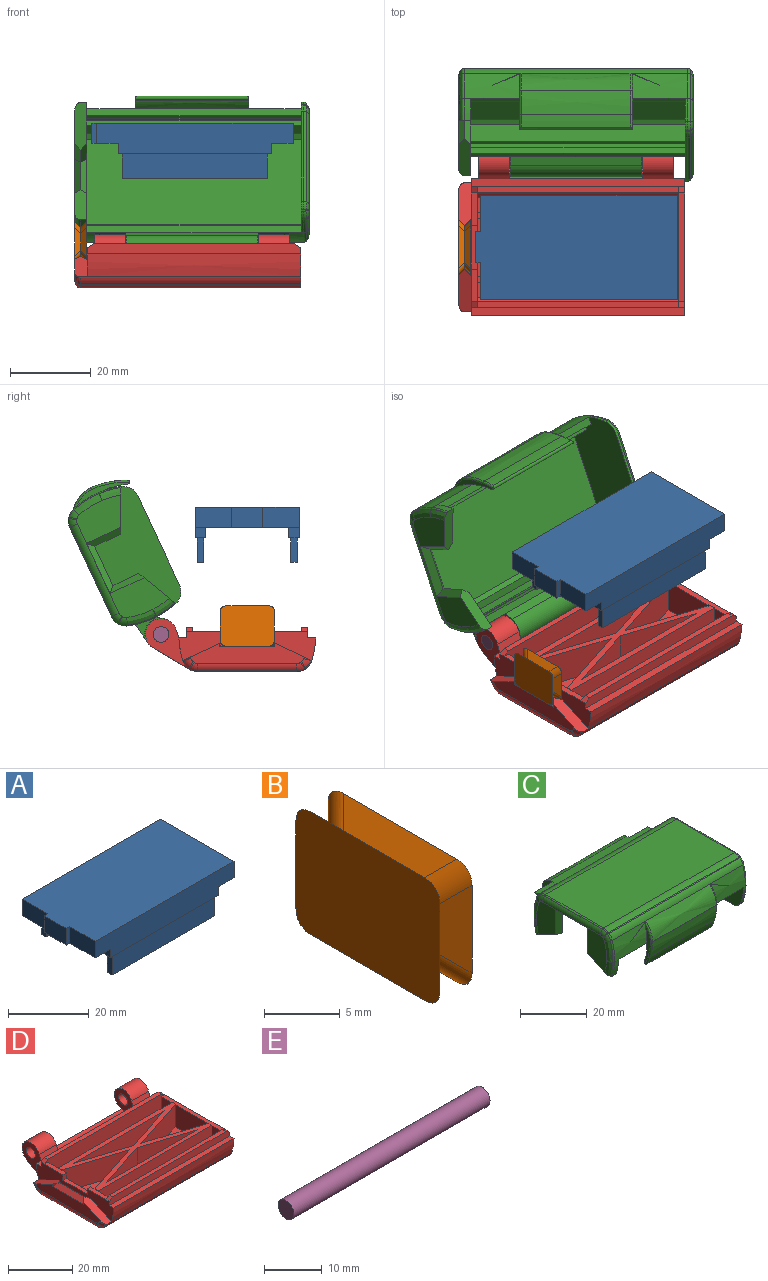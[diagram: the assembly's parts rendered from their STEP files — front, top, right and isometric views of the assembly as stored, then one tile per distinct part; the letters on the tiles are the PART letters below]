
ASSEMBLY  parts=5 mates=4
PART A: 28 faces, bbox 49.8x25.7x13.6 mm
  f0: plane 37.9x2.6mm, normal (0,0,-1), area 41.1mm2, adj f7,f12,f13,f14,f23,f24,f25,f26
  f1: plane 37.9x2.6mm, normal (0,0,-1), area 41.1mm2, adj f9,f15,f16,f17,f18,f19,f20,f21
  f2: plane 9x5mm, normal (-1,0,0), area 45mm2, adj f3,f9,f10,f11
  f3: plane 5x1.2mm, normal (0,1,0), area 6mm2, adj f2,f4,f10,f11
  f4: plane 7.7x5mm, normal (-1,0,0), area 38.5mm2, adj f3,f5,f10,f11
  f5: plane 5x1.2mm, normal (0,-1,0), area 6mm2, adj f4,f6,f10,f11
  f6: plane 9x5mm, normal (-1,0,0), area 45mm2, adj f5,f7,f10,f11
  f7: plane 48.6x7.6mm, normal (0,-1,0), area 341.5mm2, adj f0,f6,f8,f10,f11,f12,f14
  f8: plane 25.7x5mm, normal (1,0,0), area 128.5mm2, adj f7,f9,f10,f11
  f9: plane 48.6x7.6mm, normal (0,1,0), area 341.5mm2, adj f1,f2,f8,f10,f11,f15,f17
  f10: plane 49.8x25.7mm, normal (0,0,1), area 1258.3mm2, adj f2,f3,f4,f5,f6,f7,f8,f9
  f11: plane 49.8x25.7mm, normal (0,0,-1), area 1061.2mm2, adj f2,f3,f4,f5,f6,f7,f8,f9
  f12: plane 2.6x2.6mm, normal (-1,0,0), area 6.8mm2, adj f0,f7,f11,f13
  f13: plane 37.9x2.6mm, normal (0,1,0), area 98.5mm2, adj f0,f11,f12,f14
  f14: plane 2.6x2.6mm, normal (1,0,0), area 6.8mm2, adj f0,f7,f11,f13
  f15: plane 2.6x2.6mm, normal (1,0,0), area 6.8mm2, adj f1,f9,f11,f16
  f16: plane 37.9x2.6mm, normal (0,-1,0), area 98.5mm2, adj f1,f11,f15,f17
  f17: plane 2.6x2.6mm, normal (-1,0,0), area 6.8mm2, adj f1,f9,f11,f16
  f18: plane 6x1.6mm, normal (1,0,0), area 9.6mm2, adj f1,f19,f21,f22
  f19: plane 35.9x6mm, normal (0,-1,0), area 215.4mm2, adj f1,f18,f20,f22
  f20: plane 6x1.6mm, normal (-1,0,0), area 9.6mm2, adj f1,f19,f21,f22
  f21: plane 35.9x6mm, normal (0,1,0), area 215.4mm2, adj f1,f18,f20,f22
  f22: plane 35.9x1.6mm, normal (0,0,-1), area 57.4mm2, adj f18,f19,f20,f21
  f23: plane 6x1.6mm, normal (1,0,0), area 9.6mm2, adj f0,f24,f26,f27
  f24: plane 35.9x6mm, normal (0,-1,0), area 215.4mm2, adj f0,f23,f25,f27
  f25: plane 6x1.6mm, normal (-1,0,0), area 9.6mm2, adj f0,f24,f26,f27
  f26: plane 35.9x6mm, normal (0,1,0), area 215.4mm2, adj f0,f23,f25,f27
  f27: plane 35.9x1.6mm, normal (0,0,-1), area 57.4mm2, adj f23,f24,f25,f26
PART B: 23 faces, bbox 3.4x13.9x10.4 mm
  f0: plane 13.42x9.92mm, normal (-1,0,0), area 131.6mm2, adj f5,f6,f7,f8,f11,f13,f14,f16
  f1: plane 10.59x1.5mm, normal (-0.71,0,0.71), area 19.3mm2, adj f5,f9,f10,f12
  f2: plane 7.09x1.5mm, normal (-0.71,-0.71,0), area 11.9mm2, adj f6,f9,f12,f17
  f3: plane 7.09x1.5mm, normal (-0.71,0.71,0), area 11.9mm2, adj f7,f9,f10,f15
  f4: plane 10.59x1.5mm, normal (-0.71,0,-0.71), area 19.3mm2, adj f8,f9,f15,f17
  f5: plane 10.59x1.5mm, normal (0.71,0,0.71), area 19.3mm2, adj f0,f1,f11,f13
  f6: plane 7.09x1.5mm, normal (0.71,-0.71,0), area 11.9mm2, adj f0,f2,f13,f16
  f7: plane 7.09x1.5mm, normal (0.71,0.71,0), area 11.9mm2, adj f0,f3,f11,f14
  f8: plane 10.59x1.5mm, normal (0.71,0,-0.71), area 19.3mm2, adj f0,f4,f14,f16
  f9: plane 13.42x9.92mm, normal (1,0,0), area 51.1mm2, adj f1,f2,f3,f4,f10,f12,f15,f17
  f10: cylinder r=2mm len=3.13mm, axis (-0.58,-0.58,-0.58), area 5.4mm2, adj f1,f3,f9,f11
  f11: cylinder r=2mm len=3.13mm, axis (-0.58,0.58,0.58), area 5.4mm2, adj f0,f5,f7,f10
  f12: cylinder r=2mm len=3.13mm, axis (-0.58,0.58,-0.58), area 5.4mm2, adj f1,f2,f9,f13
  f13: cylinder r=2mm len=3.13mm, axis (-0.58,-0.58,0.58), area 5.4mm2, adj f0,f5,f6,f12
  f14: cylinder r=2mm len=3.13mm, axis (0.58,-0.58,0.58), area 5.4mm2, adj f0,f7,f8,f15
  f15: cylinder r=2mm len=3.13mm, axis (0.58,0.58,-0.58), area 5.4mm2, adj f3,f4,f9,f14
  f16: cylinder r=2mm len=3.13mm, axis (0.58,0.58,0.58), area 5.4mm2, adj f0,f6,f8,f17
  f17: cylinder r=2mm len=3.13mm, axis (0.58,-0.58,-0.58), area 5.4mm2, adj f2,f4,f9,f16
  f18: plane 7.4x0.75mm, normal (0.71,-0.71,0), area 7.1mm2, adj f9,f19,f21,f22
  f19: plane 9.37x5.9mm, normal (1,0,0), area 55.3mm2, adj f18,f20,f21,f22
  f20: plane 7.4x0.75mm, normal (0.71,0.71,0), area 7.1mm2, adj f9,f19,f21,f22
  f21: plane 10.87x0.75mm, normal (0.71,0,0.71), area 10.7mm2, adj f9,f18,f19,f20
  f22: plane 10.87x0.75mm, normal (0.71,0,-0.71), area 10.7mm2, adj f9,f18,f19,f20
PART C: 183 faces, bbox 58x44.2x23.5 mm
  f0: extruded ~55.38x7.38mm, area 142.9mm2, adj f15,f20,f36,f40,f92,f105,f172,f178
  f1: extruded ~14.19x7.37mm, area 102.5mm2, adj f13,f23,f26,f77,f147,f159
  f2: extruded ~14.19x7.37mm, area 102.5mm2, adj f13,f23,f43,f96,f155,f165
  f3: plane 29.75x12.79mm, normal (-1,0,0), area 170.4mm2, adj f126,f127,f128,f129,f130,f131,f132,f133
  f4: plane 53x1mm, normal (0,-1,0), area 53mm2, adj f5,f17,f38,f39
  f5: plane 53x1.5mm, normal (0,0,-1), area 79.5mm2, adj f4,f6,f38,f39
  f6: plane 53x4.6mm, normal (0,-1,0), area 243.8mm2, adj f5,f25,f38,f39
  f7: plane 53x24.9mm, normal (0,0,-1), area 1319.7mm2, adj f24,f25,f38,f39
  f8: plane 53x4.6mm, normal (0,1,0), area 243.8mm2, adj f9,f24,f38,f39
  f9: plane 53x1.5mm, normal (0,0,-1), area 79.5mm2, adj f8,f10,f38,f39
  f10: plane 53x1mm, normal (0,1,0), area 53mm2, adj f9,f11,f38,f39
  f11: plane 53x0.1mm, normal (0,0,-1), area 5.3mm2, adj f10,f12,f38,f39
  f12: plane 53x1.5mm, normal (0,1,0), area 79.5mm2, adj f11,f13,f38,f39
  f13: plane 53x1.89mm, normal (0,0,-1), area 99.9mm2, adj f1,f2,f12,f38,f39,f149
  f14: plane 55.38x24.51mm, normal (0,0,1), area 1357.2mm2, adj f21,f22,f84,f100
  f15: plane 53x1.88mm, normal (0,0,-1), area 99.9mm2, adj f0,f16,f38,f39,f174
  f16: plane 53x1.52mm, normal (0,-1,0), area 80.5mm2, adj f15,f17,f38,f39
  f17: plane 53x0.1mm, normal (0,0,-1), area 5.3mm2, adj f4,f16,f38,f39
  f18: plane 55.38x0.22mm, normal (0,-0.57,0.82), area 15.1mm2, adj f21,f23,f80,f98
  f19: plane 55.38x0.22mm, normal (0,0.57,0.82), area 15.1mm2, adj f20,f22,f88,f102
  f20: cylinder r=3.63mm len=55.38mm, axis (-1,0,0), area 133.5mm2, adj f0,f19,f90,f104
  f21: cylinder r=3.63mm len=55.38mm, axis (1,0,0), area 123.2mm2, adj f14,f18,f82,f99
  f22: cylinder r=3.63mm len=55.38mm, axis (-1,0,0), area 123.2mm2, adj f14,f19,f86,f101
  f23: cylinder r=3.63mm len=55.38mm, axis (-1,0,0), area 133.5mm2, adj f1,f2,f18,f78,f97,f150
  f24: plane 53x1mm, normal (0,0.71,-0.71), area 75mm2, adj f7,f8,f38,f39
  f25: plane 53x1mm, normal (0,-0.71,-0.71), area 75mm2, adj f6,f7,f38,f39
  f26: plane 0.71x0.11mm, normal (0,-1,-0.04), area 0.1mm2, adj f1,f27,f38,f77,f79
  f27: extruded ~5.67x0.98mm, area 4mm2, adj f26,f28,f38,f79
  f28: cylinder r=3.63mm len=1.92mm, axis (-1,0,0), area 1.7mm2, adj f27,f29,f38,f81
  f29: plane 0.69x0.22mm, normal (0,-0.57,-0.82), area 0.2mm2, adj f28,f30,f38,f83
  f30: cylinder r=3.63mm len=2.09mm, axis (-1,0,0), area 1.5mm2, adj f29,f31,f38,f85
  f31: plane 24.51x0.69mm, normal (0,0,-1), area 16.9mm2, adj f30,f32,f38,f87
  f32: cylinder r=3.63mm len=2.09mm, axis (-1,0,0), area 1.5mm2, adj f31,f33,f38,f89
  f33: plane 0.69x0.22mm, normal (0,0.57,-0.82), area 0.2mm2, adj f32,f34,f38,f91
  f34: cylinder r=3.63mm len=1.92mm, axis (-1,0,0), area 1.7mm2, adj f33,f35,f38,f93
  f35: extruded ~5.67x0.98mm, area 4mm2, adj f34,f36,f38,f94
  f36: plane 0.71x0.09mm, normal (0,1,-0.04), area 0.1mm2, adj f0,f35,f38,f92,f94
  f37: plane 29.75x14.45mm, normal (1,0,0), area 415.5mm2, adj f106,f107,f108,f109,f110,f111,f112,f113
  f38: plane 33.87x16.6mm, normal (-1,0,0), area 497.5mm2, adj f4,f5,f6,f7,f8,f9,f10,f11
  f39: plane 33.87x13.84mm, normal (1,0,0), area 185.6mm2, adj f4,f5,f6,f7,f8,f9,f10,f11
  f40: plane 1.71x0.09mm, normal (0,1,-0.04), area 0.1mm2, adj f0,f39,f41,f103,f105
  f41: extruded ~5.57x1.69mm, area 9.6mm2, adj f39,f40,f103,f146
  f42: extruded ~5.57x1.69mm, area 9.6mm2, adj f39,f43,f95,f145
  f43: plane 1.71x0.11mm, normal (0,-1,-0.04), area 0.2mm2, adj f2,f39,f42,f95,f96
  f44: plane 0.08x0.03mm, normal (-0.71,0.71,-0.03), area 0mm2, adj f45,f46,f103,f105,f131
  f45: bspline ~5.71x1.94mm, area 0.1mm2, adj f44,f103,f133,f146
  f46: bspline ~7.38x2.04mm, area 0.1mm2, adj f44,f105,f129
  f47: cone r=2.63mm half-angle=45deg, axis (1,0,0), area 0.1mm2, adj f48,f104,f127
  f48: plane 0.23x0.17mm, normal (-0.71,0.41,0.58), area 0mm2, adj f47,f49,f102,f126
  f49: cone r=2.63mm half-angle=45deg, axis (1,0,0), area 0.1mm2, adj f48,f50,f101,f128
  f50: plane 24.51x0.02mm, normal (-0.71,0,0.71), area 0.7mm2, adj f49,f51,f100,f130
  f51: cone r=2.63mm half-angle=45deg, axis (1,0,0), area 0.1mm2, adj f50,f52,f99,f132
  f52: plane 0.23x0.17mm, normal (-0.71,-0.41,0.58), area 0mm2, adj f51,f53,f98,f134
  f53: cone r=2.63mm half-angle=45deg, axis (1,0,0), area 0mm2, adj f52,f97,f135
  f54: bspline ~5.71x1.94mm, area 0.1mm2, adj f95,f138,f145
  f55: bspline ~7.37x2.03mm, area 0mm2, adj f96,f136
  f56: plane 0.11x0.03mm, normal (-0.71,-0.71,-0.03), area 0mm2, adj f95,f96,f137
  f57: plane 0.11x0.03mm, normal (0.71,-0.71,-0.03), area 0mm2, adj f77,f79,f123
  f58: bspline ~5.71x1.94mm, area 0mm2, adj f79,f125
  f59: bspline ~7.37x2.03mm, area 0mm2, adj f77,f121
  f60: cone r=2.63mm half-angle=45deg, axis (-1,0,0), area 0mm2, adj f62,f81,f124
  f61: cone r=2.63mm half-angle=45deg, axis (-1,0,0), area 0.1mm2, adj f63,f78,f119
  f62: plane 0.23x0.17mm, normal (0.71,-0.41,-0.58), area 0mm2, adj f60,f64,f83,f122
  f63: plane 0.23x0.17mm, normal (0.71,-0.41,0.58), area 0mm2, adj f61,f65,f80,f117
  f64: cone r=2.63mm half-angle=45deg, axis (-1,0,0), area 0.1mm2, adj f62,f66,f85,f120
  f65: cone r=2.63mm half-angle=45deg, axis (-1,0,0), area 0.1mm2, adj f63,f67,f82,f115
  f66: plane 24.51x0.02mm, normal (0.71,0,-0.71), area 0.7mm2, adj f64,f68,f87,f118
  f67: plane 24.51x0.02mm, normal (0.71,0,0.71), area 0.7mm2, adj f65,f69,f84,f113
  f68: cone r=2.63mm half-angle=45deg, axis (-1,0,0), area 0.1mm2, adj f66,f70,f89,f116
  f69: cone r=2.63mm half-angle=45deg, axis (-1,0,0), area 0.1mm2, adj f67,f71,f86,f111
  f70: plane 0.23x0.17mm, normal (0.71,0.41,-0.58), area 0mm2, adj f68,f72,f91,f114
  f71: plane 0.23x0.17mm, normal (0.71,0.41,0.58), area 0mm2, adj f69,f73,f88,f109
  f72: cone r=2.63mm half-angle=45deg, axis (-1,0,0), area 0.1mm2, adj f70,f93,f112
  f73: cone r=2.63mm half-angle=45deg, axis (-1,0,0), area 0mm2, adj f71,f90,f107
  f74: bspline ~5.71x1.94mm, area 0.1mm2, adj f76,f94,f110
  f75: bspline ~7.38x2.04mm, area 0.1mm2, adj f76,f92,f106
  f76: plane 0.09x0.03mm, normal (0.71,0.71,-0.03), area 0mm2, adj f74,f75,f92,f94,f108
  f77: bspline ~7.94x1.28mm, area 4.4mm2, adj f1,f26,f57,f59,f78,f79
  f78: torus R=2.88mm, axis (1,0,0), area 1.4mm2, adj f23,f61,f77,f80
  f79: bspline ~7.33x1.52mm, area 3.4mm2, adj f26,f27,f57,f58,f77,f81
  f80: cylinder r=0.75mm len=0.53mm, axis (0,-0.82,-0.57), area 0.2mm2, adj f18,f63,f78,f82
  f81: torus R=2.88mm, axis (1,0,0), area 1.4mm2, adj f28,f60,f79,f83
  f82: torus R=2.88mm, axis (1,0,0), area 1.3mm2, adj f21,f65,f80,f84
  f83: cylinder r=0.75mm len=0.53mm, axis (0,0.82,-0.57), area 0.2mm2, adj f29,f62,f81,f85
  f84: cylinder r=0.75mm len=24.51mm, axis (0,-1,0), area 14.4mm2, adj f14,f67,f82,f86
  f85: torus R=2.88mm, axis (1,0,0), area 1.3mm2, adj f30,f64,f83,f87
  f86: torus R=2.88mm, axis (1,0,0), area 1.3mm2, adj f22,f69,f84,f88
  f87: cylinder r=0.75mm len=24.51mm, axis (0,1,0), area 14.4mm2, adj f31,f66,f85,f89
  f88: cylinder r=0.75mm len=0.53mm, axis (0,-0.82,0.57), area 0.2mm2, adj f19,f71,f86,f90
  f89: torus R=2.88mm, axis (1,0,0), area 1.3mm2, adj f32,f68,f87,f91
  f90: torus R=2.88mm, axis (1,0,0), area 1.4mm2, adj f20,f73,f88,f92
  f91: cylinder r=0.75mm len=0.53mm, axis (0,0.82,0.57), area 0.2mm2, adj f33,f70,f89,f93
  f92: bspline ~8.64x1.51mm, area 4.4mm2, adj f0,f36,f75,f76,f90,f94
  f93: torus R=2.88mm, axis (1,0,0), area 1.4mm2, adj f34,f72,f91,f94
  f94: bspline ~7.35x1.4mm, area 3.4mm2, adj f35,f36,f74,f76,f92,f93
  f95: bspline ~7.35x1.4mm, area 3.3mm2, adj f42,f43,f54,f56,f96,f145
  f96: bspline ~7.94x1.28mm, area 4.4mm2, adj f2,f43,f55,f56,f95,f97
  f97: torus R=2.88mm, axis (-1,0,0), area 1.4mm2, adj f23,f53,f96,f98
  f98: cylinder r=0.75mm len=0.53mm, axis (0,0.82,0.57), area 0.2mm2, adj f18,f52,f97,f99
  f99: torus R=2.88mm, axis (-1,0,0), area 1.3mm2, adj f21,f51,f98,f100
  f100: cylinder r=0.75mm len=24.51mm, axis (0,1,0), area 14.4mm2, adj f14,f50,f99,f101
  f101: torus R=2.88mm, axis (-1,0,0), area 1.3mm2, adj f22,f49,f100,f102
  f102: cylinder r=0.75mm len=0.53mm, axis (0,0.82,-0.57), area 0.2mm2, adj f19,f48,f101,f104
  f103: bspline ~7.33x1.52mm, area 3.3mm2, adj f40,f41,f44,f45,f105,f146
  f104: torus R=2.88mm, axis (-1,0,0), area 1.4mm2, adj f20,f47,f102,f105
  f105: bspline ~8.65x1.51mm, area 4.4mm2, adj f0,f40,f44,f46,f103,f104
  f106: bspline ~9.59x3.35mm, area 14.5mm2, adj f37,f75,f107,f108
  f107: torus R=1.56mm, axis (1,0,0), area 3.4mm2, adj f37,f73,f106,f109
  f108: cylinder r=2.6mm len=1.84mm, axis (0,0.04,1), area 0.2mm2, adj f37,f76,f106,f110
  f109: cylinder r=2.6mm len=1.66mm, axis (0,-0.82,0.57), area 0.6mm2, adj f37,f71,f107,f111
  f110: bspline ~7.45x3.19mm, area 11.2mm2, adj f37,f74,f108,f112
  f111: torus R=1.56mm, axis (1,0,0), area 3.2mm2, adj f37,f69,f109,f113
  f112: torus R=1.56mm, axis (1,0,0), area 3.4mm2, adj f37,f72,f110,f114
  f113: cylinder r=2.6mm len=24.51mm, axis (0,-1,0), area 50mm2, adj f37,f67,f111,f115
  f114: cylinder r=2.6mm len=1.66mm, axis (0,0.82,0.57), area 0.6mm2, adj f37,f70,f112,f116
  f115: torus R=1.56mm, axis (1,0,0), area 3.2mm2, adj f37,f65,f113,f117
  f116: torus R=1.56mm, axis (1,0,0), area 3.2mm2, adj f37,f68,f114,f118
  f117: cylinder r=2.6mm len=1.66mm, axis (0,-0.82,-0.57), area 0.6mm2, adj f37,f63,f115,f119
  f118: cylinder r=2.6mm len=24.51mm, axis (0,1,0), area 50mm2, adj f37,f66,f116,f120
  f119: torus R=1.56mm, axis (1,0,0), area 3.4mm2, adj f37,f61,f117,f121
  f120: torus R=1.56mm, axis (1,0,0), area 3.2mm2, adj f37,f64,f118,f122
  f121: bspline ~9.61x3.35mm, area 14.5mm2, adj f37,f59,f119,f123
  f122: cylinder r=2.6mm len=1.66mm, axis (0,0.82,-0.57), area 0.6mm2, adj f37,f62,f120,f124
  f123: cylinder r=2.6mm len=1.84mm, axis (0,-0.04,1), area 0.2mm2, adj f37,f57,f121,f125
  f124: torus R=1.56mm, axis (1,0,0), area 3.4mm2, adj f37,f60,f122,f125
  f125: bspline ~7.47x3.19mm, area 11.2mm2, adj f37,f58,f123,f124
  f126: cylinder r=2.6mm len=1.66mm, axis (0,0.82,-0.57), area 0.6mm2, adj f3,f48,f127,f128
  f127: torus R=1.56mm, axis (-1,0,0), area 3.4mm2, adj f3,f47,f126,f129
  f128: torus R=1.56mm, axis (-1,0,0), area 3.2mm2, adj f3,f49,f126,f130
  f129: bspline ~11.34x3.35mm, area 14.5mm2, adj f3,f46,f127,f131
  f130: cylinder r=2.6mm len=24.51mm, axis (0,1,0), area 50mm2, adj f3,f50,f128,f132
  f131: cylinder r=2.6mm len=1.84mm, axis (0,0.04,1), area 0.2mm2, adj f3,f44,f129,f133
  f132: torus R=1.56mm, axis (-1,0,0), area 3.2mm2, adj f3,f51,f130,f134
  f133: bspline ~6.97x2.84mm, area 10.6mm2, adj f3,f45,f131,f146
  f134: cylinder r=2.6mm len=1.66mm, axis (0,0.82,0.57), area 0.6mm2, adj f3,f52,f132,f135
  f135: torus R=1.56mm, axis (-1,0,0), area 3.4mm2, adj f3,f53,f134,f136
  f136: bspline ~11.33x3.36mm, area 14.5mm2, adj f3,f55,f135,f137
  f137: cylinder r=2.6mm len=1.84mm, axis (0,-0.04,1), area 0.2mm2, adj f3,f56,f136,f138
  f138: bspline ~6.96x2.84mm, area 10.6mm2, adj f3,f54,f137,f145
  f139: plane 13.7x1.5mm, normal (-0.71,0,-0.71), area 25.9mm2, adj f3,f140,f141,f142
  f140: plane 9.31x1.5mm, normal (-0.71,0.71,0), area 17.4mm2, adj f3,f139,f143,f145
  f141: plane 9.31x1.5mm, normal (-0.71,-0.71,0), area 17.4mm2, adj f3,f139,f144,f146
  f142: plane 13.7x1.5mm, normal (0.71,0,-0.71), area 25.9mm2, adj f39,f139,f143,f144
  f143: plane 9.31x1.5mm, normal (0.71,0.71,0), area 17.4mm2, adj f39,f140,f142,f145
  f144: plane 9.31x1.5mm, normal (0.71,-0.71,0), area 17.4mm2, adj f39,f141,f142,f146
  f145: plane 10.67x5.12mm, normal (0,0.43,-0.9), area 32.2mm2, adj f3,f39,f42,f54,f95,f138,f140,f143
  f146: plane 10.67x5.11mm, normal (0,-0.43,-0.9), area 32.2mm2, adj f3,f39,f41,f45,f103,f133,f141,f144
  f147: plane 14.5x2.63mm, normal (1,0,0), area 14.2mm2, adj f1,f148,f149,f157,f159,f160,f161,f162
  f148: plane 28x0.01mm, normal (0,0.94,0.33), area 0.4mm2, adj f147,f149,f155,f157
  f149: extruded ~28x7.38mm, area 210.2mm2, adj f13,f147,f148,f155
  f150: extruded ~27x6.04mm, area 186.2mm2, adj f23,f151,f159,f165
  f151: plane 27x0.04mm, normal (0,-1,-0.04), area 0.9mm2, adj f150,f152,f160,f166
  f152: plane 27x0.04mm, normal (0,-1,-0.04), area 1.2mm2, adj f151,f153,f161,f167
  f153: plane 27x0mm, normal (0,-1,-0.04), area 0mm2, adj f152,f154,f162,f168
  f154: extruded ~27x6.09mm, area 167.1mm2, adj f153,f156,f163,f169
  f155: plane 14.5x2.63mm, normal (-1,0,0), area 14.2mm2, adj f2,f148,f149,f157,f165,f166,f167,f168
  f156: extruded ~27x2.93mm, area 84.9mm2, adj f154,f158,f164,f170
  f157: cylinder r=0.5mm len=28mm, axis (-1,0,0), area 43.5mm2, adj f147,f148,f155,f158,f164,f170
  f158: plane 27.08x0mm, normal (0,0.38,-0.92), area 0mm2, adj f156,f157,f164,f170
  f159: bspline ~6.65x3.7mm, area 4.9mm2, adj f1,f147,f150,f160
  f160: cylinder r=0.5mm len=0.5mm, axis (0,-0.04,1), area 0mm2, adj f147,f151,f159,f161
  f161: cylinder r=0.5mm len=0.5mm, axis (0,-0.04,1), area 0mm2, adj f147,f152,f160,f162
  f162: cylinder r=0.5mm len=0.5mm, axis (0,-0.04,1), area 0mm2, adj f147,f153,f161,f163
  f163: bspline ~15.73x4.09mm, area 4.8mm2, adj f147,f154,f162,f164
  f164: bspline ~5.71x2.71mm, area 2.7mm2, adj f147,f156,f157,f158,f163
  f165: bspline ~6.65x3.7mm, area 4.9mm2, adj f2,f150,f155,f166
  f166: cylinder r=0.5mm len=0.5mm, axis (0,0.04,-1), area 0mm2, adj f151,f155,f165,f167
  f167: cylinder r=0.5mm len=0.5mm, axis (0,0.04,-1), area 0mm2, adj f152,f155,f166,f168
  f168: cylinder r=0.5mm len=0.5mm, axis (0,0.04,-1), area 0mm2, adj f153,f155,f167,f169
  f169: bspline ~15.73x4.09mm, area 4.8mm2, adj f154,f155,f168,f170
  f170: bspline ~5.71x2.71mm, area 2.7mm2, adj f155,f156,f157,f158,f169
  f171: plane 8.25x7.91mm, normal (1,0,0), area 37.3mm2, adj f172,f173,f174,f179,f180,f182
  f172: plane 48x5.58mm, normal (0,0.17,0.98), area 252.6mm2, adj f0,f171,f173,f175,f177,f178,f179,f181
  f173: cylinder r=3.88mm len=32.6mm, axis (-1,0,0), area 484.2mm2, adj f171,f172,f174,f175
  f174: plane 48x1.69mm, normal (0,-0.76,-0.65), area 72.7mm2, adj f15,f171,f173,f175,f176,f178,f180,f181
  f175: plane 8.25x7.91mm, normal (-1,0,0), area 37.3mm2, adj f172,f173,f174,f176,f177,f182
  f176: plane 7.7x1.76mm, normal (0,0.97,-0.23), area 13.9mm2, adj f174,f175,f177,f178
  f177: cylinder r=4.07mm len=7.7mm, axis (-1,0,0), area 37.7mm2, adj f172,f175,f176,f178
  f178: plane 5.63x4.34mm, normal (-1,0,0), area 6.8mm2, adj f0,f172,f174,f176,f177
  f179: cylinder r=4.07mm len=7.7mm, axis (-1,0,0), area 37.7mm2, adj f171,f172,f180,f181
  f180: plane 7.7x1.76mm, normal (0,0.97,-0.23), area 13.9mm2, adj f171,f174,f179,f181
  f181: plane 5.63x4.34mm, normal (1,0,0), area 6.8mm2, adj f0,f172,f174,f179,f180
  f182: cylinder r=1.94mm len=32.6mm, axis (-1,0,0), area 396.9mm2, adj f171,f175
PART D: 113 faces, bbox 55.9x42.2x13.5 mm
  f0: plane 48x2.14mm, normal (0,-0.95,0.32), area 36mm2, adj f1,f2,f27,f105,f106,f107,f109,f110
  f1: cylinder r=3.88mm len=7.55mm, axis (-1,0,0), area 112mm2, adj f0,f3,f106,f107
  f2: cylinder r=3.88mm len=7.55mm, axis (-1,0,0), area 112mm2, adj f0,f3,f105,f109
  f3: plane 48x8.85mm, normal (0,0.51,-0.86), area 451.7mm2, adj f1,f2,f36,f105,f106,f107,f108,f109
  f4: extruded ~5.67x2.9mm, area 16.7mm2, adj f5,f20,f27,f105
  f5: cylinder r=3.63mm len=2.9mm, axis (-1,0,0), area 7mm2, adj f4,f20,f36,f105
  f6: plane 14.5x8.4mm, normal (1,0,0), area 99.3mm2, adj f13,f14,f16,f44,f45,f46,f94,f95
  f7: plane 8.4x4.7mm, normal (1,0,0), area 39mm2, adj f11,f14,f23,f43,f96
  f8: plane 8.4x4.7mm, normal (-1,0,0), area 39mm2, adj f11,f15,f23,f43,f96
  f9: plane 14.5x8.4mm, normal (-1,0,0), area 121.8mm2, adj f10,f15,f97,f98
  f10: plane 22.46x14.5mm, normal (0,0,1), area 162.8mm2, adj f9,f97,f98
  f11: plane 49.8x3.7mm, normal (0,0,1), area 184.3mm2, adj f7,f8,f43,f96
  f12: plane 49.8x3.7mm, normal (0,0,1), area 184.3mm2, adj f22,f24,f42,f93
  f13: plane 22.46x14.5mm, normal (0,0,1), area 162.8mm2, adj f6,f94,f95
  f14: plane 8.1x1.5mm, normal (0,0,1), area 12.2mm2, adj f6,f7,f18,f23,f46,f87
  f15: plane 26.9x1.5mm, normal (0,0,1), area 40.4mm2, adj f8,f9,f20,f23,f24,f25,f88,f89
  f16: plane 8.1x1.5mm, normal (0,0,1), area 12.2mm2, adj f6,f18,f22,f25,f44,f86
  f17: plane 52.8x2.5mm, normal (0,-1,0), area 130.5mm2, adj f18,f20,f29,f31,f34,f35
  f18: plane 33.86x7.24mm, normal (-1,0,0), area 121.7mm2, adj f14,f16,f17,f19,f26,f27,f28,f29
  f19: plane 52.8x2.5mm, normal (0,1,0), area 130.5mm2, adj f18,f20,f27,f30,f32,f33
  f20: plane 33.86x9.9mm, normal (1,0,0), area 314.3mm2, adj f4,f5,f15,f17,f19,f21,f27,f28
  f21: plane 54.59x24.51mm, normal (0,0,-1), area 1337.8mm2, adj f20,f40,f41,f63
  f22: plane 8.4x4.7mm, normal (1,0,0), area 39mm2, adj f12,f16,f25,f42,f93
  f23: plane 52.8x8.4mm, normal (0,1,0), area 419.8mm2, adj f7,f8,f14,f15,f31,f34,f35,f43
  f24: plane 8.4x4.7mm, normal (-1,0,0), area 39mm2, adj f12,f15,f25,f42,f93
  f25: plane 52.8x8.4mm, normal (0,-1,0), area 419.8mm2, adj f15,f16,f22,f24,f30,f32,f33,f42
  f26: extruded ~5.67x1.9mm, area 11mm2, adj f18,f27,f39,f106
  f27: plane 52.8x1.98mm, normal (0,0,1), area 104.6mm2, adj f0,f4,f18,f19,f20,f26
  f28: extruded ~52.8x5.67mm, area 304.4mm2, adj f18,f20,f29,f38
  f29: plane 52.8x1.98mm, normal (0,0,1), area 104.6mm2, adj f17,f18,f20,f28
  f30: plane 49.8x1.5mm, normal (0,0,1), area 74.7mm2, adj f19,f25,f32,f33
  f31: plane 49.8x1.5mm, normal (0,0,1), area 74.7mm2, adj f17,f23,f34,f35
  f32: plane 1.5x1.5mm, normal (0.55,0,0.83), area 2.7mm2, adj f19,f20,f25,f30
  f33: plane 1.5x1.5mm, normal (-0.55,0,0.83), area 2.7mm2, adj f18,f19,f25,f30
  f34: plane 1.5x1.5mm, normal (-0.55,0,0.83), area 2.7mm2, adj f17,f18,f23,f31
  f35: plane 1.5x1.5mm, normal (0.55,0,0.83), area 2.7mm2, adj f17,f20,f23,f31
  f36: plane 54.59x0.22mm, normal (0,0.57,-0.82), area 8mm2, adj f3,f5,f20,f39,f40,f65,f105,f106
  f37: plane 54.59x0.22mm, normal (0,-0.57,-0.82), area 14.9mm2, adj f20,f38,f41,f61
  f38: cylinder r=3.63mm len=54.59mm, axis (-1,0,0), area 131.6mm2, adj f20,f28,f37,f47,f60
  f39: cylinder r=3.63mm len=3.69mm, axis (-1,0,0), area 8.9mm2, adj f26,f36,f48,f66,f106
  f40: cylinder r=3.63mm len=54.59mm, axis (1,0,0), area 121.5mm2, adj f20,f21,f36,f64
  f41: cylinder r=3.63mm len=54.59mm, axis (-1,0,0), area 121.5mm2, adj f20,f21,f37,f62
  f42: plane 49.8x1mm, normal (0,-0.71,0.71), area 70.4mm2, adj f12,f22,f24,f25
  f43: plane 49.8x1mm, normal (0,0.71,0.71), area 70.4mm2, adj f7,f8,f11,f23
  f44: plane 2.1x1.5mm, normal (0,-1,0), area 3.2mm2, adj f6,f16,f18,f45
  f45: plane 10.7x1.5mm, normal (0,0,1), area 16.1mm2, adj f6,f18,f44,f46
  f46: plane 2.1x1.5mm, normal (0,1,0), area 3.2mm2, adj f6,f14,f18,f45
  f47: plane 10.64x5.1mm, normal (0,-0.43,0.9), area 33.1mm2, adj f18,f38,f49,f58,f59,f73,f77,f79
  f48: plane 10.64x5.1mm, normal (0,0.43,0.9), area 33.1mm2, adj f18,f39,f49,f50,f67,f68,f78,f81
  f49: plane 28.11x5.01mm, normal (-1,0,0), area 103.7mm2, adj f47,f48,f68,f69,f70,f71,f72,f73
  f50: bspline ~5.71x1.94mm, area 0mm2, adj f48,f67,f68
  f51: cone r=2.63mm half-angle=45deg, axis (1,0,0), area 0mm2, adj f52,f66,f69
  f52: plane 0.23x0.17mm, normal (-0.71,0.41,-0.58), area 0mm2, adj f51,f53,f65,f70
  f53: cone r=2.63mm half-angle=45deg, axis (1,0,0), area 0.1mm2, adj f52,f54,f64,f71
  f54: plane 24.51x0.02mm, normal (-0.71,0,-0.71), area 0.7mm2, adj f53,f55,f63,f72
  f55: cone r=2.63mm half-angle=45deg, axis (1,0,0), area 0.1mm2, adj f54,f56,f62,f74
  f56: plane 0.23x0.17mm, normal (-0.71,-0.41,-0.58), area 0mm2, adj f55,f57,f61,f76
  f57: cone r=2.63mm half-angle=45deg, axis (1,0,0), area 0.1mm2, adj f56,f60,f75
  f58: bspline ~5.71x1.94mm, area 0mm2, adj f47,f59,f73
  f59: bspline ~1.48x0.63mm, area 0mm2, adj f47,f58,f60
  f60: torus R=2.88mm, axis (-1,0,0), area 1.4mm2, adj f38,f57,f59,f61
  f61: cylinder r=0.75mm len=0.53mm, axis (0,-0.82,0.57), area 0.2mm2, adj f37,f56,f60,f62
  f62: torus R=2.88mm, axis (-1,0,0), area 1.3mm2, adj f41,f55,f61,f63
  f63: cylinder r=0.75mm len=24.51mm, axis (0,-1,0), area 14.4mm2, adj f21,f54,f62,f64
  f64: torus R=2.88mm, axis (-1,0,0), area 1.3mm2, adj f40,f53,f63,f65
  f65: cylinder r=0.75mm len=0.53mm, axis (0,-0.82,-0.57), area 0.2mm2, adj f36,f52,f64,f66
  f66: torus R=2.88mm, axis (-1,0,0), area 1.4mm2, adj f39,f51,f65,f67
  f67: bspline ~1.94x0.77mm, area 0mm2, adj f48,f50,f66
  f68: bspline ~2.9x2.46mm, area 0.4mm2, adj f48,f49,f50,f69
  f69: torus R=1.56mm, axis (-1,0,0), area 3.4mm2, adj f49,f51,f68,f70
  f70: cylinder r=2.6mm len=1.66mm, axis (0,-0.82,-0.57), area 0.6mm2, adj f49,f52,f69,f71
  f71: torus R=1.56mm, axis (-1,0,0), area 3.2mm2, adj f49,f53,f70,f72
  f72: cylinder r=2.6mm len=24.51mm, axis (0,-1,0), area 50mm2, adj f49,f54,f71,f74
  f73: bspline ~2.51x2.36mm, area 0.4mm2, adj f47,f49,f58,f75
  f74: torus R=1.56mm, axis (-1,0,0), area 3.2mm2, adj f49,f55,f72,f76
  f75: torus R=1.56mm, axis (-1,0,0), area 3.4mm2, adj f49,f57,f73,f76
  f76: cylinder r=2.6mm len=1.66mm, axis (0,-0.82,0.57), area 0.6mm2, adj f49,f56,f74,f75
  f77: plane 1.5x1.5mm, normal (-0.71,0.71,0), area 0.8mm2, adj f47,f49,f80
  f78: plane 1.5x1.5mm, normal (-0.71,-0.71,0), area 0.8mm2, adj f48,f49,f80
  f79: plane 1.5x1.5mm, normal (0.71,0.71,0), area 0.8mm2, adj f47,f82,f85
  f80: plane 13.7x1.5mm, normal (-0.71,0,0.71), area 25.9mm2, adj f49,f77,f78,f82
  f81: plane 1.5x1.5mm, normal (0.71,-0.71,0), area 0.8mm2, adj f48,f82,f83
  f82: plane 13.7x1.5mm, normal (0.71,0,0.71), area 25.9mm2, adj f79,f80,f81,f84
  f83: plane 0.78x0.1mm, normal (0,-1,0), area 0.1mm2, adj f18,f48,f81,f84
  f84: plane 13.7x0.1mm, normal (0,0,1), area 1.4mm2, adj f18,f82,f83,f85
  f85: plane 0.78x0.1mm, normal (0,1,0), area 0.1mm2, adj f18,f47,f79,f84
  f86: plane 1.5x0.2mm, normal (-1,0,0), area 0.3mm2, adj f16,f90,f93,f94
  f87: plane 1.5x0.2mm, normal (-1,0,0), area 0.3mm2, adj f14,f90,f95,f96
  f88: plane 1.5x0.2mm, normal (1,0,0), area 0.3mm2, adj f15,f90,f96,f97
  f89: plane 1.5x0.2mm, normal (1,0,0), area 0.3mm2, adj f15,f90,f93,f98
  f90: plane 49.8x17.5mm, normal (0,0,1), area 287.2mm2, adj f86,f87,f88,f89,f91,f92,f93,f94
  f91: plane 20.02x8.6mm, normal (-0.31,-0.95,0), area 180.9mm2, adj f90,f92,f102,f103
  f92: plane 40.03x8.6mm, normal (0,1,0), area 344.3mm2, adj f90,f91,f102,f103
  f93: plane 49.8x8.6mm, normal (0,1,0), area 428.3mm2, adj f12,f22,f24,f86,f89,f90
  f94: plane 22.46x8.6mm, normal (-0.31,-0.95,0), area 203mm2, adj f6,f13,f86,f90,f95
  f95: plane 22.46x8.6mm, normal (-0.31,0.95,0), area 203mm2, adj f6,f13,f87,f90,f94
  f96: plane 49.8x8.6mm, normal (0,-1,0), area 428.3mm2, adj f7,f8,f11,f87,f88,f90
  f97: plane 22.46x8.6mm, normal (0.31,0.95,0), area 203mm2, adj f9,f10,f88,f90,f98
  f98: plane 22.46x8.6mm, normal (0.31,-0.95,0), area 203mm2, adj f9,f10,f89,f90,f97
  f99: plane 20.02x8.6mm, normal (0.31,0.95,0), area 180.9mm2, adj f90,f100,f101,f104
  f100: plane 40.03x8.6mm, normal (0,-1,0), area 344.3mm2, adj f90,f99,f101,f104
  f101: plane 20.02x8.6mm, normal (-0.31,0.95,0), area 180.9mm2, adj f90,f99,f100,f104
  f102: plane 20.02x8.6mm, normal (0.31,-0.95,0), area 180.9mm2, adj f90,f91,f92,f103
  f103: plane 40.03x6.46mm, normal (0,0,1), area 129.3mm2, adj f91,f92,f102
  f104: plane 40.03x6.46mm, normal (0,0,1), area 129.3mm2, adj f99,f100,f101
  f105: plane 12.44x10.75mm, normal (1,0,0), area 52.8mm2, adj f0,f2,f3,f4,f5,f36,f111
  f106: plane 12.44x10.75mm, normal (-1,0,0), area 52.8mm2, adj f0,f1,f3,f26,f36,f39,f112
  f107: plane 8.25x7.95mm, normal (1,0,0), area 37.3mm2, adj f0,f1,f3,f108,f110,f112
  f108: cylinder r=4.07mm len=33mm, axis (1,0,0), area 188.2mm2, adj f3,f107,f109,f110
  f109: plane 8.25x7.95mm, normal (-1,0,0), area 37.3mm2, adj f0,f2,f3,f108,f110,f111
  f110: plane 33x0.71mm, normal (0,0.76,0.65), area 30.8mm2, adj f0,f107,f108,f109
  f111: cylinder r=1.94mm len=7.5mm, axis (-1,0,0), area 91.3mm2, adj f105,f109
  f112: cylinder r=1.94mm len=7.5mm, axis (-1,0,0), area 91.3mm2, adj f106,f107
PART E: 3 faces, bbox 48x3.9x3.9 mm
  f0: plane 3.88x3.88mm, normal (1,0,0), area 11.8mm2, adj f2
  f1: plane 3.88x3.88mm, normal (-1,0,0), area 11.8mm2, adj f2
  f2: cylinder r=1.94mm len=48mm, axis (-1,0,0), area 584.3mm2, adj f0,f1
PLACE A t=(3.36,-1.55,26.2)mm
PLACE B t=(3.14,-1.55,0.53)mm
PLACE C rot(axis=(-1,0,0),115deg) t=(3.14,29.51,18.75)mm
PLACE D t=(3.14,-1.55,0.56)mm fixed
PLACE E t=(3.14,-1.55,0.56)mm
MATE revolute C.f173 <-> D.f1  axis (-1,0,0) through (18.94,19.77,-0.24)mm
MATE slider D.f90 <-> A.f11  axis (0,0,1) through (3.14,-1.55,0.56)mm
MATE revolute E.f2 <-> D.f1  axis (-1,0,0) through (-21.36,19.77,-0.24)mm
MATE planar B.f0 <-> D.f49  axis (-1,0,0) through (-26.36,-1.55,1.83)mm
